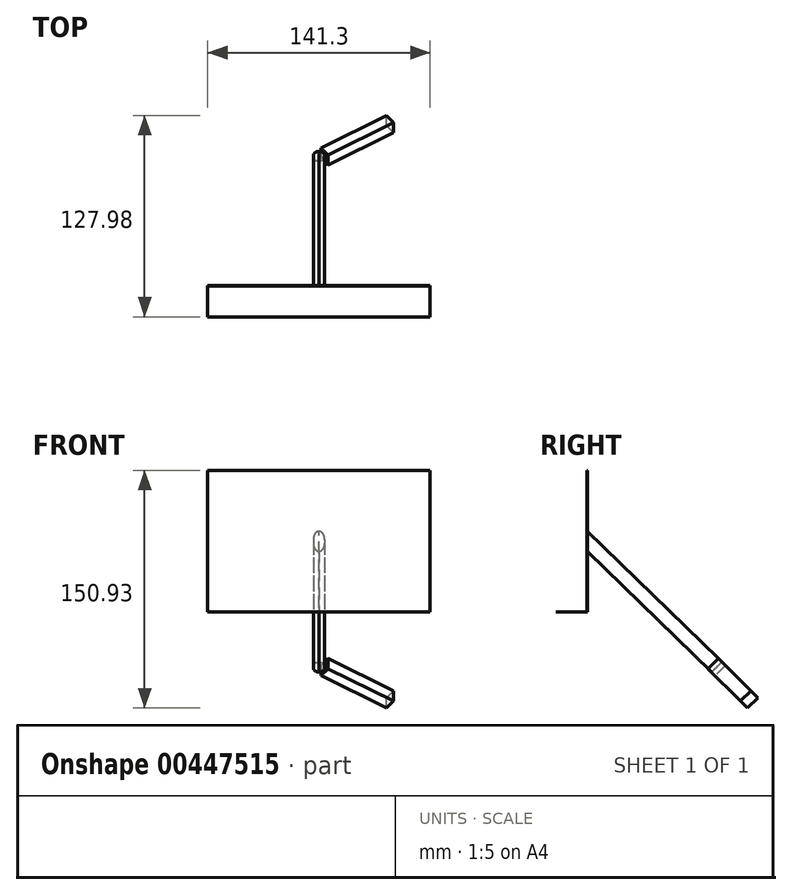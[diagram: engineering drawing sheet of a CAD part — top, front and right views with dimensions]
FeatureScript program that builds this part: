
annotation { "Feature Type Name" : "Feature", "Feature Type Description" : "" }
export const myFeature = defineFeature(function(context is Context, id is Id, definition is map)
    precondition{}
    {
        {
            var Q0;
            Q0=qCreatedBy(makeId("Front.planeOp"),FACE);
            var sketch = newSketch(context, id + "F0", { "sketchPlane" : qUnion([Q0])});
            skLineSegment(sketch, "E0.bottom", {"start": v(70.65, 45) * mm, "end": v(-70.65, 45) * mm});
            skLineSegment(sketch, "E0.top", {"start": v(70.65, -45) * mm, "end": v(-70.65, -45) * mm});
            skLineSegment(sketch, "E0.left", {"start": v(70.65, 45) * mm, "end": v(70.65, -45) * mm});
            skLineSegment(sketch, "E0.right", {"start": v(-70.65, 45) * mm, "end": v(-70.65, -45) * mm});
            skPoint(sketch, "E0.middle", {"position": v(0, 0) * mm});
            skSolve(sketch);
        }
        {
            var Q0;
            Q0=makeQuery(id+"F0.imprint","IMPRINT",FACE,{"disambiguationData":[TD([[makeQuery(id+"F0.imprint","IMPRINT",EDGE,{"derivedFrom":sQuery(id+"F0.wireOp",EDGE,"E0.bottom")}),1.0]])]});
            extrude(context, id + "F1", {"entities" : qUnion([Q0]), "depth" : 0.25 * mm});
        }
        {
            var Q0;
            Q0=makeQuery(id+"F1.opExtrude","CAP_FACE",FACE,{"disambiguationData":[OSD([sQuery(id+"F0.wireOp",EDGE,"E0.bottom"),sQuery(id+"F0.wireOp",EDGE,"E0.top"),sQuery(id+"F0.wireOp",EDGE,"E0.left"),sQuery(id+"F0.wireOp",EDGE,"E0.right")])],"isStart":false});
            var sketch = newSketch(context, id + "F2", { "sketchPlane" : qUnion([Q0])});
            skLineSegment(sketch, "E1.0", {"start": v(70.65, -45) * mm, "end": v(-70.65, -45) * mm});
            skLineSegment(sketch, "E2", {"start": v(-70.65, -45) * mm, "end": v(-70.65, -44.74) * mm});
            skLineSegment(sketch, "E3", {"start": v(-70.65, -44.74) * mm, "end": v(70.65, -44.74) * mm});
            skLineSegment(sketch, "E4", {"start": v(70.65, -44.74) * mm, "end": v(70.65, -45) * mm});
            skSolve(sketch);
        }
        {
            var Q0;
            Q0 = qSketchRegion(id + "F2", true);
            extrude(context, id + "F3", {"entities" : qUnion([Q0]), "operationType" : NewBodyOperationType.ADD, "depth" : 19.56 * mm});
        }
        {
            var Q0;
            Q0=qCreatedBy(makeId("Right.planeOp"),FACE);
            var sketch = newSketch(context, id + "F4", { "sketchPlane" : qUnion([Q0])});
            skLineSegment(sketch, "E5", {"start": v(0, 6.35) * mm, "end": v(0, -6.35) * mm});
            skLineSegment(sketch, "E6", {"start": v(0, -6.35) * mm, "end": v(78.92, -83.12) * mm});
            skLineSegment(sketch, "E7", {"start": v(0, 6.35) * mm, "end": v(85.36, -76.68) * mm});
            skLineSegment(sketch, "E8", {"start": v(85.36, -76.68) * mm, "end": v(78.92, -83.12) * mm});
            skSolve(sketch);
        }
        {
            var Q0;
            Q0=makeQuery(id+"F4.imprint","IMPRINT",FACE,{"disambiguationData":[TD([[makeQuery(id+"F4.imprint","IMPRINT",EDGE,{"derivedFrom":sQuery(id+"F4.wireOp",EDGE,"E5")}),1.0]])]});
            extrude(context, id + "F5", {"entities" : qUnion([Q0]), "operationType" : NewBodyOperationType.ADD, "endBound" : BoundingType.SYMMETRIC, "depth" : 7.11 * mm});
        }
        {
            var Q0;
            Q0=makeQuery(id+"F5.opExtrude","CAP_EDGE",EDGE,{"disambiguationData":[OSD([sQuery(id+"F4.wireOp",EDGE,"E8")])],"isStart":false});
            cPlane(context, id + "F6", {"entities" : qUnion([Q0]), "cplaneType" : CPlaneType.LINE_ANGLE, "offset" : 25.4 * mm, "angle" : 145 * degree, "width" : 152.4 * mm, "height" : 152.4 * mm});
        }
        {
            var Q0;
            Q0=qCreatedBy(id+"F6.planeOp",FACE);
            var sketch = newSketch(context, id + "F7", { "sketchPlane" : qUnion([Q0])});
            skLineSegment(sketch, "E9.0", {"start": v(68.63, 6.15) * mm, "end": v(68.63, -2.95) * mm});
            skLineSegment(sketch, "E10", {"start": v(68.63, -2.95) * mm, "end": v(119.43, -2.95) * mm});
            skLineSegment(sketch, "E11", {"start": v(119.43, -2.95) * mm, "end": v(119.43, 6.15) * mm});
            skLineSegment(sketch, "E12", {"start": v(119.43, 6.15) * mm, "end": v(68.63, 6.15) * mm});
            skSolve(sketch);
        }
        {
            var Q0;
            Q0=makeQuery(id+"F7.imprint","IMPRINT",FACE,{"disambiguationData":[TD([[makeQuery(id+"F7.imprint","IMPRINT",EDGE,{"derivedFrom":sQuery(id+"F7.wireOp",EDGE,"E9.0")}),1.0]])]});
            extrude(context, id + "F8", {"entities" : qUnion([Q0]), "endBound" : BoundingType.SYMMETRIC, "depth" : 7.62 * mm});
        }
        {
            var Q0;
            Q0=makeQuery(id+"F5.opExtrude","CAP_EDGE",EDGE,{"disambiguationData":[OSD([sQuery(id+"F4.wireOp",EDGE,"E7")])],"isStart":true});
            var Q1;
            Q1=makeQuery(id+"F5.opExtrude","CAP_EDGE",EDGE,{"disambiguationData":[OSD([sQuery(id+"F4.wireOp",EDGE,"E6")])],"isStart":true});
            var Q2;
            Q2=makeQuery(id+"F5.opExtrude","CAP_EDGE",EDGE,{"disambiguationData":[OSD([sQuery(id+"F4.wireOp",EDGE,"E7")])],"isStart":false});
            var Q3;
            Q3=makeQuery(id+"F5.opExtrude","CAP_EDGE",EDGE,{"disambiguationData":[OSD([sQuery(id+"F4.wireOp",EDGE,"E6")])],"isStart":false});
            fillet(context, id + "F9", {"entities" : qUnion([Q0, Q1, Q2, Q3]), "radius" : 3.68 * mm, "tangentPropagation" : true, "allowEdgeOverflow" : false});
        }
    });
